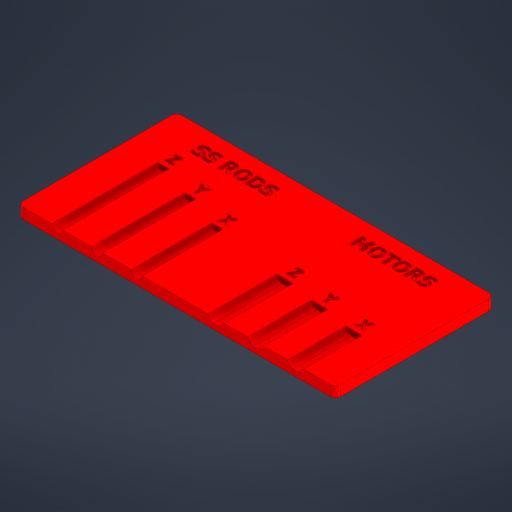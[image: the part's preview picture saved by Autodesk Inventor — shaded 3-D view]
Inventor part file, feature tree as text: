
AUTODESK INVENTOR PART (.ipt)
format: ipt  version: 2023.4 (Build 274418000, 418)  size: 660,480 bytes
history: native  units: mm
features: extrude x3, sketch x2, fillet x1, projected_geometry x1
ambient origin geometry x8: Origin, YZ Plane, XZ Plane, XY Plane, X Axis, Y Axis, Z Axis, Center Point
bodies: Solid1 (feature_tree)
feature tree (7):
  sketch  "Sketch1"  dims[d0=150.0mm d1=75.0mm]
  extrude  "Extrusion1"  Depth=75.0mm
  extrude  "Extrusion2"  Depth=44.0mm
  extrude  "Extrusion3"  Depth=38.0mm
  fillet  "Fillet1"  Radius=32.5mm
  sketch  "Sketch2"  dims[d2=50.0mm d3=44.0mm d4=38.0mm d5=32.5mm d6=30.0mm d7=27.5mm d8=5.0mm d9=5.0mm d10=5.0mm d11=7.5mm d12=7.5mm d13=7.5mm d14=5.0mm d15=0.0mm d16=2.5mm d17=0.0mm d18=10.0mm d19=50.0mm d20=10.0mm d21=10.0mm d22=50.0mm d23=10.0mm d24=7.5mm d25=7.5mm d26=7.5mm d27=7.5mm d28=7.5mm d29=7.5mm d30=1.25mm d31=0.0mm d32=2.5mm]
  projected_geometry  "Projected Loop1"
